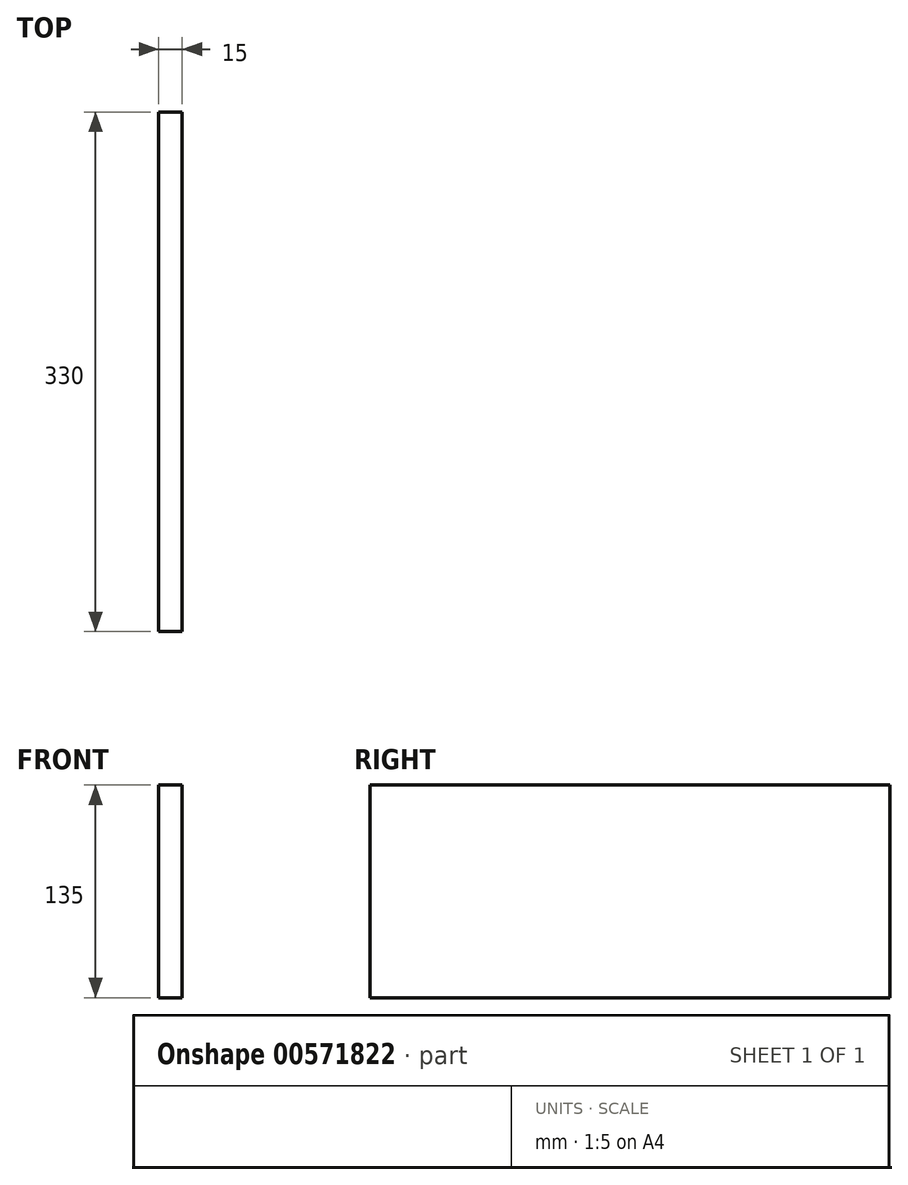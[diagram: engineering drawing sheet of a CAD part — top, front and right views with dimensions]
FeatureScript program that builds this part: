
annotation { "Feature Type Name" : "Feature", "Feature Type Description" : "" }
export const myFeature = defineFeature(function(context is Context, id is Id, definition is map)
    precondition{}
    {
        {
            var Q0;
            Q0=qCreatedBy(makeId("Front.planeOp"),FACE);
            var sketch = newSketch(context, id + "F0", { "sketchPlane" : qUnion([Q0])});
            skLineSegment(sketch, "E0.bottom", {"start": v(-1.38, 0) * mm, "end": v(-16.38, 0) * mm});
            skLineSegment(sketch, "E0.top", {"start": v(-1.38, 135) * mm, "end": v(-16.38, 135) * mm});
            skLineSegment(sketch, "E0.left", {"start": v(-1.38, 0) * mm, "end": v(-1.38, 135) * mm});
            skLineSegment(sketch, "E0.right", {"start": v(-16.38, 0) * mm, "end": v(-16.38, 135) * mm});
            skSolve(sketch);
        }
        {
            var Q0;
            Q0=makeQuery(id+"F0.imprint","IMPRINT",FACE,{"disambiguationData":[TD([[makeQuery(id+"F0.imprint","IMPRINT",EDGE,{"derivedFrom":sQuery(id+"F0.wireOp",EDGE,"E0.bottom")}),-1.0]])]});
            extrude(context, id + "F1", {"entities" : qUnion([Q0]), "oppositeDirection" : true, "depth" : 330 * mm, "offsetDistance" : 25 * mm});
        }
    });
